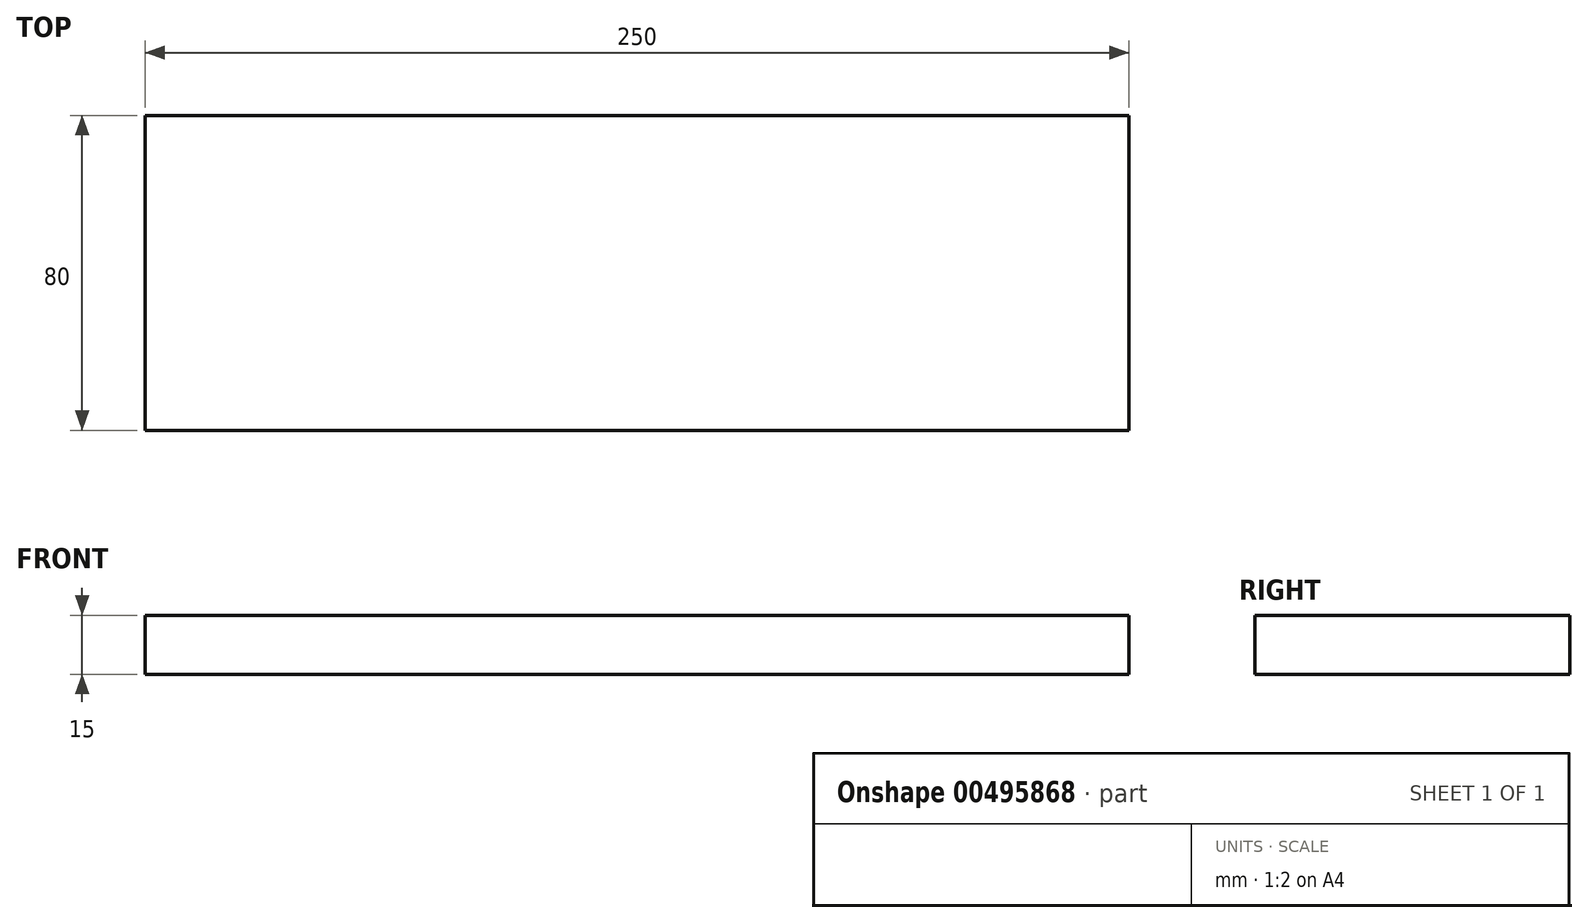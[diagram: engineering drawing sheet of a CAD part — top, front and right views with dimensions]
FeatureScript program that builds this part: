
annotation { "Feature Type Name" : "Feature", "Feature Type Description" : "" }
export const myFeature = defineFeature(function(context is Context, id is Id, definition is map)
    precondition{}
    {
        {
            var Q0;
            Q0=qCreatedBy(makeId("Top.planeOp"),FACE);
            var sketch = newSketch(context, id + "F0", { "sketchPlane" : qUnion([Q0])});
            skLineSegment(sketch, "E0.bottom", {"start": v(125, 40) * mm, "end": v(-125, 40) * mm});
            skLineSegment(sketch, "E0.top", {"start": v(125, -40) * mm, "end": v(-125, -40) * mm});
            skLineSegment(sketch, "E0.left", {"start": v(125, 40) * mm, "end": v(125, -40) * mm});
            skLineSegment(sketch, "E0.right", {"start": v(-125, 40) * mm, "end": v(-125, -40) * mm});
            skPoint(sketch, "E0.middle", {"position": v(0, 0) * mm});
            skSolve(sketch);
        }
        {
            var Q0;
            Q0=qSketchRegion(id+"F0",true);
            extrude(context, id + "F1", {"entities" : qUnion([Q0]), "depth" : 15 * mm});
        }
    });
